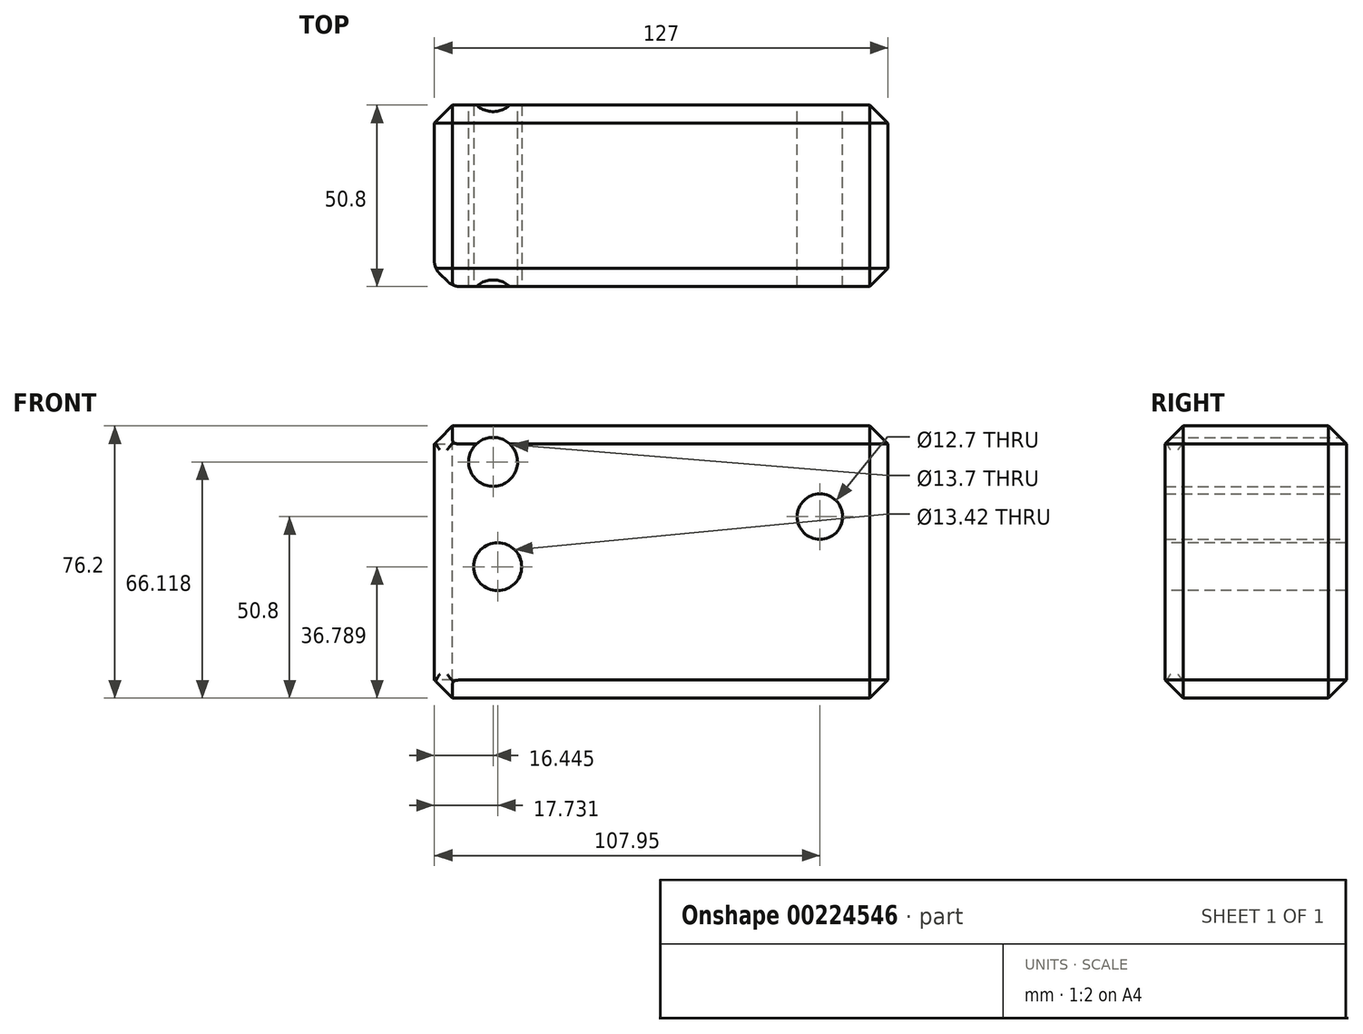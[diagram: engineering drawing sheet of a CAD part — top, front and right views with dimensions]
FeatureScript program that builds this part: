
annotation { "Feature Type Name" : "Feature", "Feature Type Description" : "" }
export const myFeature = defineFeature(function(context is Context, id is Id, definition is map)
    precondition{}
    {
        {
            var Q0;
            Q0=qCreatedBy(makeId("Front.planeOp"),FACE);
            var sketch = newSketch(context, id + "F0", { "sketchPlane" : qUnion([Q0])});
            skLineSegment(sketch, "E0.bottom", {"start": v(-127, 76.2) * mm, "end": v(0, 76.2) * mm});
            skLineSegment(sketch, "E0.top", {"start": v(-127, 0) * mm, "end": v(0, 0) * mm});
            skLineSegment(sketch, "E0.left", {"start": v(-127, 76.2) * mm, "end": v(-127, 0) * mm});
            skLineSegment(sketch, "E0.right", {"start": v(0, 76.2) * mm, "end": v(0, 0) * mm});
            skCircle(sketch, "E1", {"center": v(-19.05, 50.8) * mm, "radius": 6.35 * mm});
            skCircle(sketch, "E2", {"center": v(-110.56, 66.12) * mm, "radius": 6.85 * mm});
            skSolve(sketch);
        }
        {
            var Q0;
            Q0=makeQuery(id+"F0.imprint","IMPRINT",FACE,{"disambiguationData":[TD([[makeQuery(id+"F0.imprint","IMPRINT",EDGE,{"derivedFrom":sQuery(id+"F0.wireOp",EDGE,"E0.bottom")}),-1.0]])]});
            extrude(context, id + "F1", {"entities" : qUnion([Q0]), "depth" : 50.8 * mm});
        }
        {
            var Q0;
            Q0=makeQuery(id+"F1.opExtrude","CAP_FACE",FACE,{"disambiguationData":[OSD([sQuery(id+"F0.wireOp",EDGE,"E0.bottom"),sQuery(id+"F0.wireOp",EDGE,"E0.top"),sQuery(id+"F0.wireOp",EDGE,"E0.left"),sQuery(id+"F0.wireOp",EDGE,"E0.right"),sQuery(id+"F0.wireOp",EDGE,"E1"),sQuery(id+"F0.wireOp",EDGE,"E2")])],"isStart":false});
            var sketch = newSketch(context, id + "F2", { "sketchPlane" : qUnion([Q0])});
            skCircle(sketch, "E3", {"center": v(-109.27, 36.79) * mm, "radius": 6.7 * mm});
            skSolve(sketch);
        }
        {
            var Q0;
            Q0=makeQuery(id+"F2.imprint","IMPRINT",FACE,{"disambiguationData":[TD([[makeQuery(id+"F2.imprint","IMPRINT",EDGE,{"derivedFrom":sQuery(id+"F2.wireOp",EDGE,"E3")}),1.0]])]});
            extrude(context, id + "F3", {"entities" : qUnion([Q0]), "operationType" : NewBodyOperationType.REMOVE, "oppositeDirection" : true, "depth" : 127 * mm});
        }
        {
            var Q0;
            Q0=makeQuery(id+"F1.opExtrude","CAP_EDGE",EDGE,{"disambiguationData":[OSD([sQuery(id+"F0.wireOp",EDGE,"E0.left")])],"isStart":false});
            var Q1;
            Q1=makeQuery(id+"F1.opExtrude","CAP_EDGE",EDGE,{"disambiguationData":[OSD([sQuery(id+"F0.wireOp",EDGE,"E0.bottom")])],"isStart":false});
            var Q2;
            Q2=makeQuery(id+"F1.opExtrude","CAP_EDGE",EDGE,{"disambiguationData":[OSD([sQuery(id+"F0.wireOp",EDGE,"E0.left")])],"isStart":true});
            var Q3;
            Q3=makeQuery(id+"F1.opExtrude","CAP_EDGE",EDGE,{"disambiguationData":[OSD([sQuery(id+"F0.wireOp",EDGE,"E0.bottom")])],"isStart":true});
            var Q4;
            Q4=makeQuery(id+"F1.opExtrude","SWEPT_EDGE",EDGE,{"disambiguationData":[OSD([sQuery(id+"F0.wireOp",EDGE,"E0.top"),sQuery(id+"F0.wireOp",EDGE,"E0.left")])]});
            var Q5;
            Q5=makeQuery(id+"F1.opExtrude","SWEPT_EDGE",EDGE,{"disambiguationData":[OSD([sQuery(id+"F0.wireOp",EDGE,"E0.bottom"),sQuery(id+"F0.wireOp",EDGE,"E0.left")])]});
            var Q6;
            Q6=makeQuery(id+"F1.opExtrude","CAP_EDGE",EDGE,{"disambiguationData":[OSD([sQuery(id+"F0.wireOp",EDGE,"E0.top")])],"isStart":true});
            var Q7;
            Q7=makeQuery(id+"F1.opExtrude","SWEPT_EDGE",EDGE,{"disambiguationData":[OSD([sQuery(id+"F0.wireOp",EDGE,"E0.top"),sQuery(id+"F0.wireOp",EDGE,"E0.right")])]});
            var Q8;
            Q8=makeQuery(id+"F1.opExtrude","CAP_EDGE",EDGE,{"disambiguationData":[OSD([sQuery(id+"F0.wireOp",EDGE,"E0.top")])],"isStart":false});
            var Q9;
            Q9=makeQuery(id+"F1.opExtrude","SWEPT_FACE",FACE,{"disambiguationData":[OSD([sQuery(id+"F0.wireOp",EDGE,"E0.bottom")])]});
            var Q10;
            Q10=makeQuery(id+"F1.opExtrude","CAP_EDGE",EDGE,{"disambiguationData":[OSD([sQuery(id+"F0.wireOp",EDGE,"E0.right")])],"isStart":false});
            var Q11;
            Q11=makeQuery(id+"F1.opExtrude","CAP_EDGE",EDGE,{"disambiguationData":[OSD([sQuery(id+"F0.wireOp",EDGE,"E0.right")])],"isStart":true});
            chamfer(context, id + "F4", {"entities" : qUnion([Q0, Q1, Q2, Q3, Q4, Q5, Q6, Q7, Q8, Q9, Q10, Q11]), "width" : 5.08 * mm, "tangentPropagation" : true});
        }
        {
            var Q0;
            {var subQ0=sQuery(id+"F0.wireOp",EDGE,"E0.left");Q0=makeQuery(id+"F4.opChamfer","BLEND_FACE",FACE,{"disambiguationData":[OSD([subQ0]),TDD([makeQuery(id+"F1.opExtrude","CAP_EDGE",EDGE,{"disambiguationData":[OSD([subQ0])],"isStart":false})])]});}
            fillet(context, id + "F5", {"entities" : qUnion([Q0]), "radius" : 5.08 * mm, "tangentPropagation" : true, "allowEdgeOverflow" : false});
        }
    });
